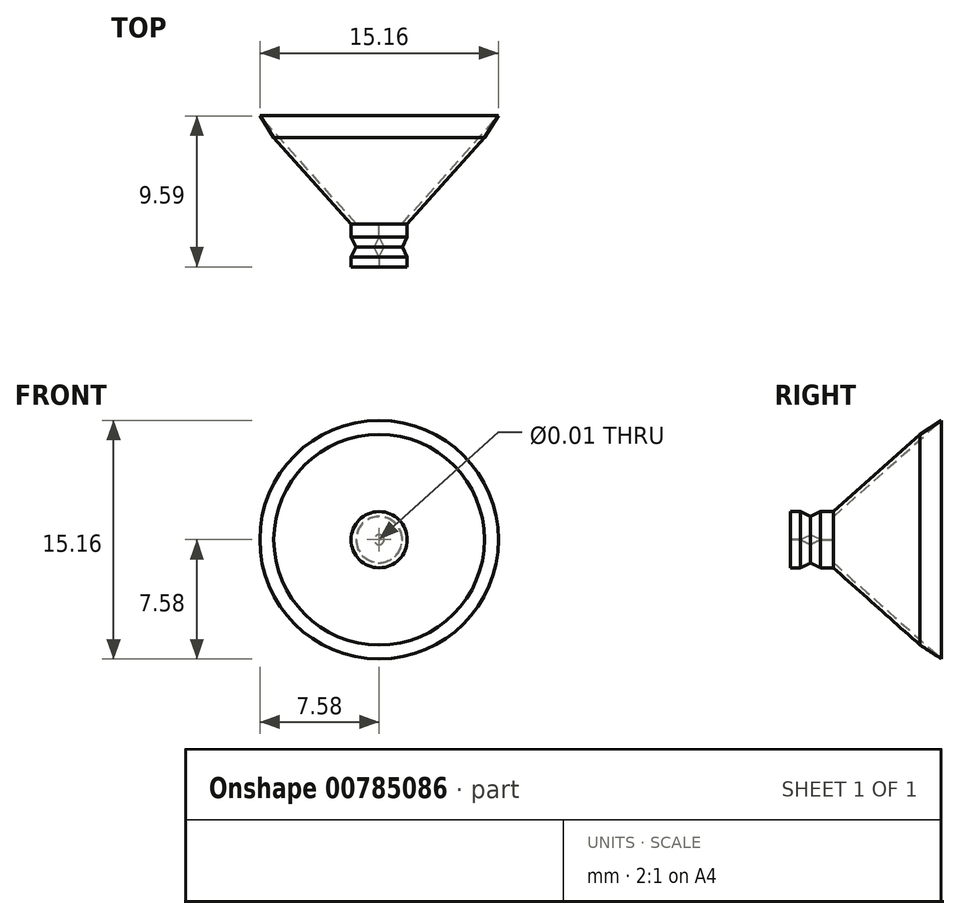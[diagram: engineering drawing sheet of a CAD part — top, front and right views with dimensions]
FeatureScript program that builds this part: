
annotation { "Feature Type Name" : "Feature", "Feature Type Description" : "" }
export const myFeature = defineFeature(function(context is Context, id is Id, definition is map)
    precondition{}
    {
        {
            var Q0;
            Q0=qCreatedBy(makeId("Top.planeOp"),FACE);
            var sketch = newSketch(context, id + "F0", { "sketchPlane" : qUnion([Q0])});
            skLineSegment(sketch, "E0", {"start": v(-52.17, 24.63) * mm, "end": v(-46.04, 17.76) * mm});
            skLineSegment(sketch, "E1", {"start": v(-46.04, 17.76) * mm, "end": v(-44.6, 17.76) * mm});
            skLineSegment(sketch, "E2", {"start": v(-46.38, 17.76) * mm, "end": v(-51.28, 23.26) * mm});
            skLineSegment(sketch, "E3", {"start": v(-51.28, 23.26) * mm, "end": v(-52.17, 24.63) * mm});
            skLineSegment(sketch, "E4", {"start": v(-46.38, 15.68) * mm, "end": v(-46.38, 15.04) * mm});
            skLineSegment(sketch, "E5", {"start": v(-44.6, 15.68) * mm, "end": v(-44.6, 15.04) * mm});
            skLineSegment(sketch, "E6", {"start": v(-44.6, 15.04) * mm, "end": v(-46.38, 15.04) * mm});
            skPoint(sketch, "E7.orphan", {"position": v(-46.38, 16.31) * mm});
            skPoint(sketch, "E8.start.orphan", {"position": v(-45.49, 15.04) * mm});
            skLineSegment(sketch, "E9", {"start": v(-44.6, 15.04) * mm, "end": v(-44.6, 15.14) * mm});
            skLineSegment(sketch, "E10", {"start": v(-46.38, 16.95) * mm, "end": v(-46.07, 16.31) * mm});
            skLineSegment(sketch, "E11", {"start": v(-46.07, 16.31) * mm, "end": v(-46.38, 15.68) * mm});
            skLineSegment(sketch, "E12", {"start": v(-44.6, 16.95) * mm, "end": v(-44.9, 16.31) * mm});
            skPoint(sketch, "E12.endSnap0", {"position": v(-44.9, 16.31) * mm});
            skLineSegment(sketch, "E13", {"start": v(-44.9, 16.31) * mm, "end": v(-44.6, 15.68) * mm});
            skPoint(sketch, "E14.trimOffspring.end.orphan", {"position": v(-44.6, 17.58) * mm});
            skPoint(sketch, "E15.end.orphan", {"position": v(-46.38, 17.58) * mm});
            skLineSegment(sketch, "E16", {"start": v(-46.38, 17.76) * mm, "end": v(-46.38, 16.95) * mm});
            skLineSegment(sketch, "E17", {"start": v(-44.6, 17.76) * mm, "end": v(-44.6, 16.95) * mm});
            skSolve(sketch);
        }
        {
            var Q0;
            Q0 = qSketchRegion(id + "F0", true);
            var Q1;
            Q1=sQuery(id+"F0.wireOp",EDGE,"E9");
            revolve(context, id + "F1", {"surfaceOperationType" : NewSurfaceOperationType.NEW, "entities" : qUnion([Q0]), "axis" : qUnion([Q1]), "revolveType" : RevolveType.FULL});
        }
    });
